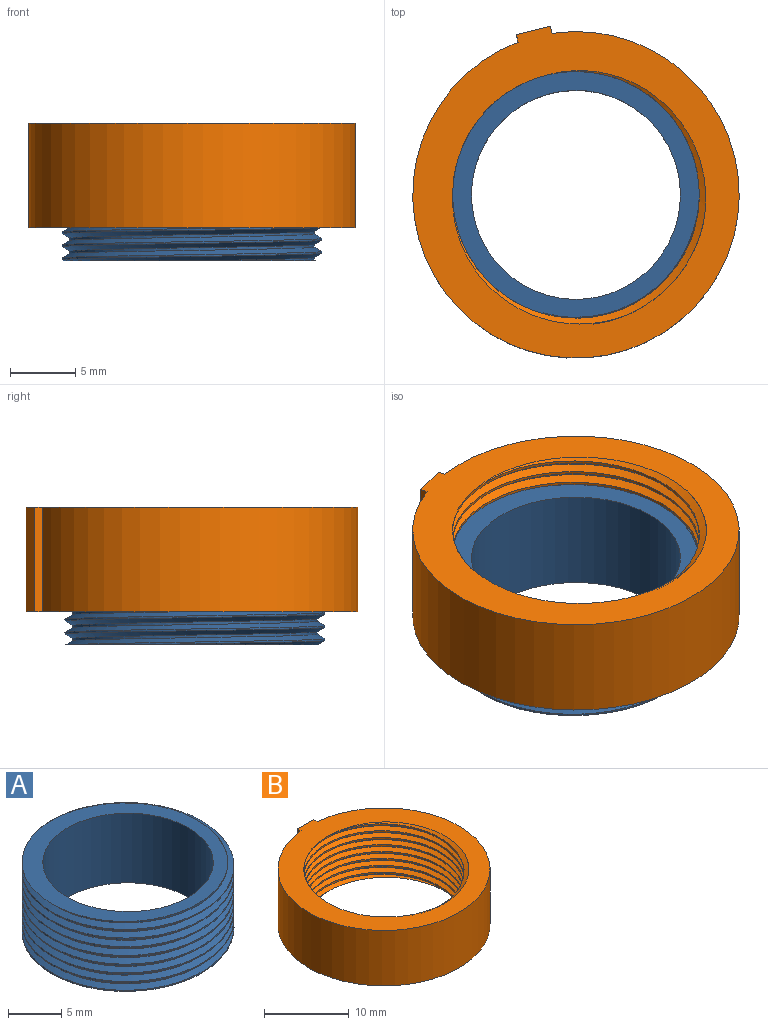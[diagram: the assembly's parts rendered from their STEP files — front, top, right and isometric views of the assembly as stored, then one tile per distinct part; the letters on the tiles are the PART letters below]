
ASSEMBLY  parts=2 mates=1
PART A: 7 faces, bbox 23.6x20.4x10.1 mm
  f0: cylinder r=9.95mm len=19.9mm, axis (0,0,-1), area 69mm2, adj f2,f3,f4,f6
  f1: cylinder r=8mm len=16mm, axis (0,0,-1), area 402.1mm2, adj f2,f3
  f2: plane 19.6x19.6mm, normal (0,0,-1), area 91.2mm2, adj f0,f1,f4,f5,f6
  f3: plane 19.6x19.6mm, normal (0,0,1), area 91.2mm2, adj f0,f1,f4,f5,f6
  f4: bspline ~23.25x20.13mm, area 323.3mm2, adj f0,f2,f3,f5
  f5: cylinder r=9.37mm len=18.75mm, axis (0,0,1), area 59.6mm2, adj f2,f3,f4,f6
  f6: bspline ~19.84x19.8mm, area 343.5mm2, adj f0,f2,f3,f5
PART B: 10 faces, bbox 25.4x25.9x9.4 mm
  f0: cylinder r=9.44mm len=18.89mm, axis (0,0,-1), area 95.5mm2, adj f5,f6,f7,f9
  f1: plane 8x0.59mm, normal (-1,0,0), area 4.7mm2, adj f2,f4,f5,f6
  f2: cylinder r=12.5mm len=25mm, axis (0,0,-1), area 606.7mm2, adj f1,f3,f5,f6
  f3: plane 8x0.58mm, normal (1,0,0), area 4.6mm2, adj f2,f4,f5,f6
  f4: plane 8x2.69mm, normal (0,1,0), area 21.5mm2, adj f1,f3,f5,f6
  f5: plane 25.88x25.37mm, normal (0,0,-1), area 196.2mm2, adj f0,f1,f2,f3,f4,f7,f8,f9
  f6: plane 25.88x25.37mm, normal (0,0,1), area 196.2mm2, adj f0,f1,f2,f3,f4,f7,f8,f9
  f7: bspline ~23.09x20mm, area 314.2mm2, adj f0,f5,f6,f8
  f8: cylinder r=10mm len=20mm, axis (0,0,1), area 95.7mm2, adj f5,f6,f7,f9
  f9: bspline ~23.09x20mm, area 314.9mm2, adj f0,f5,f6,f8
PLACE A t=(-14.35,-10.66,-6.42)mm fixed
PLACE B rot(axis=(0,0,1),14.4deg) t=(-38.57,-16.86,-3.88)mm
MATE cylindrical B.f0 <-> A.f0  axis (0,0,1) through (-14.35,-10.66,4.12)mm
